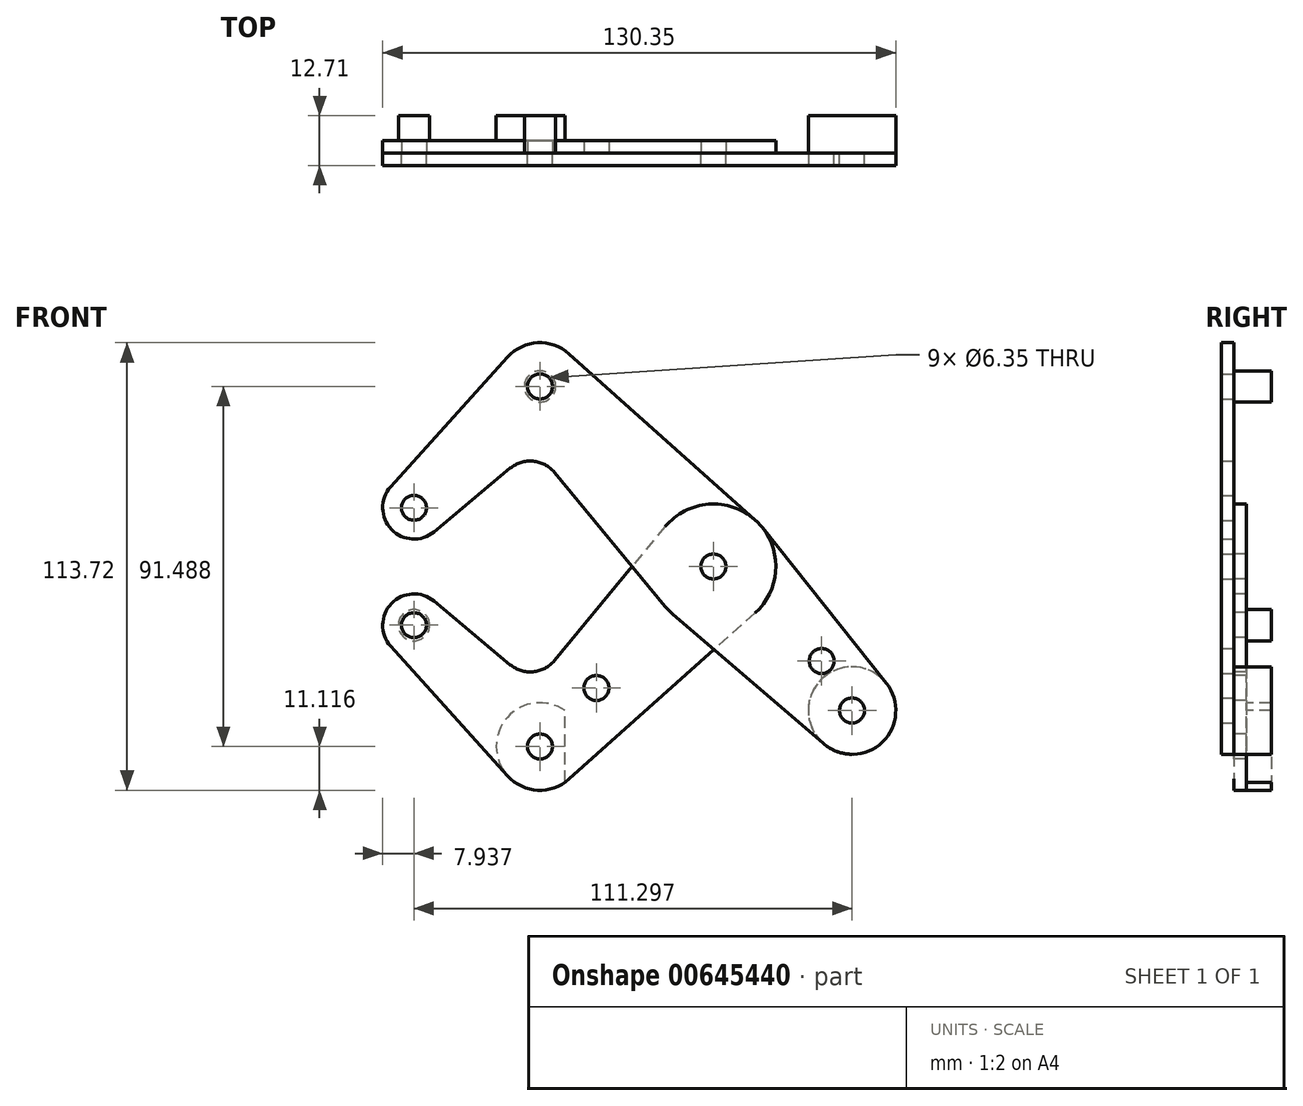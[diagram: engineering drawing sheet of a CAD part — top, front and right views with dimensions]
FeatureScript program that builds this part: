
annotation { "Feature Type Name" : "Feature", "Feature Type Description" : "" }
export const myFeature = defineFeature(function(context is Context, id is Id, definition is map)
    precondition{}
    {
        {
            var Q0;
            Q0=qCreatedBy(makeId("Front.planeOp"),FACE);
            var sketch = newSketch(context, id + "F0", { "sketchPlane" : qUnion([Q0])});
            skCircle(sketch, "E0", {"center": v(0, 0) * mm, "radius": 15.88 * mm});
            skCircle(sketch, "E1", {"center": v(0, 0) * mm, "radius": 3.98 * mm});
            skCircle(sketch, "E2", {"center": v(0, 0) * mm, "radius": 3.18 * mm});
            skCircle(sketch, "E3", {"center": v(-44.04, 45.74) * mm, "radius": 11.11 * mm});
            skCircle(sketch, "E4", {"center": v(-44.04, 45.74) * mm, "radius": 3.18 * mm});
            skCircle(sketch, "E5", {"center": v(-76.06, 14.91) * mm, "radius": 7.94 * mm});
            skCircle(sketch, "E6", {"center": v(-76.06, 14.91) * mm, "radius": 3.18 * mm});
            skCircle(sketch, "E7", {"center": v(35.23, -36.6) * mm, "radius": 11.11 * mm});
            skCircle(sketch, "E8", {"center": v(35.23, -36.6) * mm, "radius": 3.18 * mm});
            skLineSegment(sketch, "E9", {"start": v(-76.06, 14.91) * mm, "end": v(-44.04, 45.74) * mm, "construction": true});
            skLineSegment(sketch, "E10", {"start": v(-44.04, 45.74) * mm, "end": v(35.23, -36.6) * mm, "construction": true});
            skCircle(sketch, "E11", {"center": v(27.52, -24.01) * mm, "radius": 3.18 * mm});
            skLineSegment(sketch, "E12", {"start": v(-81.96, 20.22) * mm, "end": v(-52.3, 53.18) * mm});
            skLineSegment(sketch, "E13", {"start": v(-70.98, 8.82) * mm, "end": v(-51.62, 24.96) * mm});
            skLineSegment(sketch, "E14", {"start": v(-36.64, 54.03) * mm, "end": v(10.58, 11.84) * mm});
            skLineSegment(sketch, "E15", {"start": v(-40.4, 23.92) * mm, "end": v(-12.23, -10.12) * mm});
            skLineSegment(sketch, "E16", {"start": v(-10.35, -12.03) * mm, "end": v(27.99, -45.02) * mm});
            skLineSegment(sketch, "E17", {"start": v(12.42, 9.9) * mm, "end": v(43.93, -29.67) * mm});
            skLineSegment(sketch, "E18", {"start": v(0, 0) * mm, "end": v(-44.04, -45.74) * mm, "construction": true});
            skLineSegment(sketch, "E19", {"start": v(-44.04, -45.74) * mm, "end": v(-76.06, -14.91) * mm, "construction": true});
            skCircle(sketch, "E20", {"center": v(-44.04, -45.74) * mm, "radius": 11.11 * mm});
            skCircle(sketch, "E21", {"center": v(-44.04, -45.74) * mm, "radius": 3.18 * mm});
            skCircle(sketch, "E22", {"center": v(-76.06, -14.91) * mm, "radius": 7.94 * mm});
            skCircle(sketch, "E23", {"center": v(-76.06, -14.91) * mm, "radius": 3.18 * mm});
            skCircle(sketch, "E24", {"center": v(-29.72, -30.87) * mm, "radius": 3.18 * mm});
            skLineSegment(sketch, "E25", {"start": v(-81.96, -20.22) * mm, "end": v(-52.3, -53.18) * mm});
            skLineSegment(sketch, "E26", {"start": v(-70.98, -8.82) * mm, "end": v(-51.62, -24.96) * mm});
            skArc(sketch, "E27.filletArc", {"start": v(-40.4, 23.92) * mm, "mid": v(-45.8, 26.77) * mm, "end": v(-51.62, 24.96) * mm});
            skLineSegment(sketch, "E28", {"start": v(-12.23, 10.12) * mm, "end": v(-40.4, -23.92) * mm});
            skLineSegment(sketch, "E29", {"start": v(10.58, -11.84) * mm, "end": v(-36.64, -54.03) * mm});
            skArc(sketch, "E30.filletArc", {"start": v(-51.62, -24.96) * mm, "mid": v(-45.8, -26.77) * mm, "end": v(-40.4, -23.92) * mm});
            skSolve(sketch);
        }
        {
            var Q0;
            {var subQ0=sQuery(id+"F0.wireOp",EDGE,"E12");Q0=makeQuery(id+"F0.imprint","IMPRINT",FACE,{"disambiguationData":[TD([[makeQuery(id+"F0.imprint","IMPRINT",EDGE,{"derivedFrom":subQ0}),-1.0]])]});}
            var Q1;
            Q1=makeQuery(id+"F0.imprint","IMPRINT",FACE,{"disambiguationData":[TD([[makeQuery(id+"F0.imprint","IMPRINT",EDGE,{"derivedFrom":sQuery(id+"F0.wireOp",EDGE,"E6")}),-1.0]])]});
            var Q2;
            {var subQ0=sQuery(id+"F0.wireOp",EDGE,"E15");var subQ1=sQuery(id+"F0.wireOp",EDGE,"E0");var subQ2=makeQuery(id+"F0.imprint","INTERSECT",VERTEX,{"derivedFrom":[subQ1,subQ0]});Q2=makeQuery(id+"F0.imprint","IMPRINT",FACE,{"disambiguationData":[TD([[makeQuery(id+"F0.imprint","IMPRINT",EDGE,{"disambiguationData":[TD([[subQ2,1.0]])],"derivedFrom":subQ1}),-1.0]])]});}
            var Q3;
            {var subQ0=sQuery(id+"F0.wireOp",EDGE,"E16");var subQ1=sQuery(id+"F0.wireOp",EDGE,"E0");var subQ2=makeQuery(id+"F0.imprint","INTERSECT",VERTEX,{"derivedFrom":[subQ1,subQ0]});Q3=makeQuery(id+"F0.imprint","IMPRINT",FACE,{"disambiguationData":[TD([[makeQuery(id+"F0.imprint","IMPRINT",EDGE,{"disambiguationData":[TD([[subQ2,-1.0]])],"derivedFrom":subQ1}),-1.0]])]});}
            var Q4;
            Q4=makeQuery(id+"F0.imprint","IMPRINT",FACE,{"disambiguationData":[TD([[makeQuery(id+"F0.imprint","IMPRINT",EDGE,{"derivedFrom":sQuery(id+"F0.wireOp",EDGE,"E1")}),-1.0]])]});
            var Q5;
            Q5=makeQuery(id+"F0.imprint","IMPRINT",FACE,{"disambiguationData":[TD([[makeQuery(id+"F0.imprint","IMPRINT",EDGE,{"derivedFrom":sQuery(id+"F0.wireOp",EDGE,"E1")}),1.0]])]});
            var Q6;
            Q6=makeQuery(id+"F0.imprint","IMPRINT",FACE,{"disambiguationData":[TD([[makeQuery(id+"F0.imprint","IMPRINT",EDGE,{"derivedFrom":sQuery(id+"F0.wireOp",EDGE,"E11")}),-1.0]])]});
            var Q7;
            Q7=makeQuery(id+"F0.imprint","IMPRINT",FACE,{"disambiguationData":[TD([[makeQuery(id+"F0.imprint","IMPRINT",EDGE,{"derivedFrom":sQuery(id+"F0.wireOp",EDGE,"E8")}),-1.0]])]});
            var Q8;
            Q8=makeQuery(id+"F0.imprint","IMPRINT",FACE,{"disambiguationData":[TD([[makeQuery(id+"F0.imprint","IMPRINT",EDGE,{"derivedFrom":sQuery(id+"F0.wireOp",EDGE,"E4")}),-1.0]])]});
            extrude(context, id + "F1", {"entities" : qUnion([Q0, Q1, Q2, Q3, Q4, Q5, Q6, Q7, Q8]), "depth" : 3.17 * mm, "offsetDistance" : 25.4 * mm});
        }
        {
            var Q0;
            Q0=makeQuery(id+"F0.imprint","IMPRINT",FACE,{"disambiguationData":[TD([[makeQuery(id+"F0.imprint","IMPRINT",EDGE,{"derivedFrom":sQuery(id+"F0.wireOp",EDGE,"E23")}),-1.0]])]});
            var Q1;
            Q1=makeQuery(id+"F0.imprint","IMPRINT",FACE,{"disambiguationData":[TD([[makeQuery(id+"F0.imprint","IMPRINT",EDGE,{"derivedFrom":sQuery(id+"F0.wireOp",EDGE,"E24")}),-1.0]])]});
            var Q2;
            Q2=makeQuery(id+"F0.imprint","IMPRINT",FACE,{"disambiguationData":[TD([[makeQuery(id+"F0.imprint","IMPRINT",EDGE,{"derivedFrom":sQuery(id+"F0.wireOp",EDGE,"E21")}),-1.0]])]});
            var Q3;
            {var subQ0=sQuery(id+"F0.wireOp",EDGE,"E16");var subQ1=sQuery(id+"F0.wireOp",EDGE,"E0");var subQ2=makeQuery(id+"F0.imprint","INTERSECT",VERTEX,{"derivedFrom":[subQ1,subQ0]});Q3=makeQuery(id+"F0.imprint","IMPRINT",FACE,{"disambiguationData":[TD([[makeQuery(id+"F0.imprint","IMPRINT",EDGE,{"disambiguationData":[TD([[subQ2,-1.0]])],"derivedFrom":subQ1}),-1.0]])]});}
            var Q4;
            {var subQ0=sQuery(id+"F0.wireOp",EDGE,"E15");var subQ1=sQuery(id+"F0.wireOp",EDGE,"E0");var subQ2=makeQuery(id+"F0.imprint","INTERSECT",VERTEX,{"derivedFrom":[subQ1,subQ0]});Q4=makeQuery(id+"F0.imprint","IMPRINT",FACE,{"disambiguationData":[TD([[makeQuery(id+"F0.imprint","IMPRINT",EDGE,{"disambiguationData":[TD([[subQ2,1.0]])],"derivedFrom":subQ1}),-1.0]])]});}
            var Q5;
            Q5=makeQuery(id+"F0.imprint","IMPRINT",FACE,{"disambiguationData":[TD([[makeQuery(id+"F0.imprint","IMPRINT",EDGE,{"derivedFrom":sQuery(id+"F0.wireOp",EDGE,"E1")}),-1.0]])]});
            var Q6;
            Q6=makeQuery(id+"F0.imprint","IMPRINT",FACE,{"disambiguationData":[TD([[makeQuery(id+"F0.imprint","IMPRINT",EDGE,{"derivedFrom":sQuery(id+"F0.wireOp",EDGE,"E1")}),1.0]])]});
            extrude(context, id + "F2", {"entities" : qUnion([Q0, Q1, Q2, Q3, Q4, Q5, Q6]), "oppositeDirection" : true, "depth" : 3.17 * mm, "offsetDistance" : 25.4 * mm});
        }
        {
            var Q0;
            Q0=makeQuery(id+"F1.opExtrude","CAP_FACE",FACE,{"disambiguationData":[OSD([sQuery(id+"F0.wireOp",EDGE,"E0"),sQuery(id+"F0.wireOp",EDGE,"E2"),sQuery(id+"F0.wireOp",EDGE,"E3"),sQuery(id+"F0.wireOp",EDGE,"E4"),sQuery(id+"F0.wireOp",EDGE,"E5"),sQuery(id+"F0.wireOp",EDGE,"E6"),sQuery(id+"F0.wireOp",EDGE,"E7"),sQuery(id+"F0.wireOp",EDGE,"E8"),sQuery(id+"F0.wireOp",EDGE,"E11"),sQuery(id+"F0.wireOp",EDGE,"E12"),sQuery(id+"F0.wireOp",EDGE,"E13"),sQuery(id+"F0.wireOp",EDGE,"E14"),sQuery(id+"F0.wireOp",EDGE,"E15"),sQuery(id+"F0.wireOp",EDGE,"E16"),sQuery(id+"F0.wireOp",EDGE,"E17"),sQuery(id+"F0.wireOp",EDGE,"E27.filletArc")])],"isStart":false});
            var sketch = newSketch(context, id + "F3", { "sketchPlane" : qUnion([Q0])});
            skCircle(sketch, "E31", {"center": v(-44.04, 45.74) * mm, "radius": 3.98 * mm});
            skCircle(sketch, "E32.0", {"center": v(35.23, -36.6) * mm, "radius": 11.11 * mm});
            skSolve(sketch);
        }
        {
            var Q0;
            Q0=makeQuery(id+"F0.imprint","IMPRINT",FACE,{"disambiguationData":[TD([[makeQuery(id+"F0.imprint","IMPRINT",EDGE,{"derivedFrom":sQuery(id+"F0.wireOp",EDGE,"E23")}),-1.0]])]});
            var sketch = newSketch(context, id + "F4", { "sketchPlane" : qUnion([Q0])});
            skCircle(sketch, "E33", {"center": v(-76.06, -14.91) * mm, "radius": 3.98 * mm});
            skArc(sketch, "E34.0", {"start": v(-37.7, -36.62) * mm, "mid": v(-55.16, -45.74) * mm, "end": v(-37.7, -54.86) * mm});
            skLineSegment(sketch, "E35", {"start": v(-44.04, -45.74) * mm, "end": v(35.23, -36.6) * mm, "construction": true});
            skLineSegment(sketch, "E36", {"start": v(-37.7, -36.62) * mm, "end": v(-37.7, -54.86) * mm});
            skSolve(sketch);
        }
        {
            var Q0;
            Q0=qCreatedBy(makeId("Front.planeOp"),FACE);
            cPlane(context, id + "F5", {"entities" : qUnion([Q0]), "cplaneType" : CPlaneType.OFFSET, "offset" : 9.52 * mm, "oppositeDirection" : true, "width" : 152.4 * mm, "height" : 152.4 * mm});
        }
        {
            var Q0;
            Q0 = qSketchRegion(id + "F3", true);
            var Q1;
            Q1 = qSketchRegion(id + "F4", true);
            var Q2;
            Q2=qCreatedBy(id+"F5.planeOp",FACE);
            extrude(context, id + "F6", {"entities" : qUnion([Q0, Q1]), "endBound" : BoundingType.UP_TO_SURFACE, "oppositeDirection" : true, "depth" : 25.4 * mm, "endBoundEntityFace" : qUnion([Q2]), "offsetDistance" : 25.4 * mm});
        }
        {
            var Q0;
            Q0=makeQuery(id+"F1.opExtrude","SWEPT_BODY",BODY,{"disambiguationData":[OSD([sQuery(id+"F0.wireOp",EDGE,"E0"),sQuery(id+"F0.wireOp",EDGE,"E2"),sQuery(id+"F0.wireOp",EDGE,"E3"),sQuery(id+"F0.wireOp",EDGE,"E4"),sQuery(id+"F0.wireOp",EDGE,"E5"),sQuery(id+"F0.wireOp",EDGE,"E6"),sQuery(id+"F0.wireOp",EDGE,"E7"),sQuery(id+"F0.wireOp",EDGE,"E8"),sQuery(id+"F0.wireOp",EDGE,"E11"),sQuery(id+"F0.wireOp",EDGE,"E12"),sQuery(id+"F0.wireOp",EDGE,"E13"),sQuery(id+"F0.wireOp",EDGE,"E14"),sQuery(id+"F0.wireOp",EDGE,"E15"),sQuery(id+"F0.wireOp",EDGE,"E16"),sQuery(id+"F0.wireOp",EDGE,"E17"),sQuery(id+"F0.wireOp",EDGE,"E27.filletArc")])]});
            var Q1;
            Q1=makeQuery(id+"F2.opExtrude","SWEPT_BODY",BODY,{"disambiguationData":[OSD([sQuery(id+"F0.wireOp",EDGE,"E0"),sQuery(id+"F0.wireOp",EDGE,"E2"),sQuery(id+"F0.wireOp",EDGE,"E20"),sQuery(id+"F0.wireOp",EDGE,"E21"),sQuery(id+"F0.wireOp",EDGE,"E22"),sQuery(id+"F0.wireOp",EDGE,"E23"),sQuery(id+"F0.wireOp",EDGE,"E24"),sQuery(id+"F0.wireOp",EDGE,"E25"),sQuery(id+"F0.wireOp",EDGE,"E26"),sQuery(id+"F0.wireOp",EDGE,"E28"),sQuery(id+"F0.wireOp",EDGE,"E29"),sQuery(id+"F0.wireOp",EDGE,"E30.filletArc")])]});
            var Q2;
            Q2=makeQuery(id+"F6.opExtrude","SWEPT_BODY",BODY,{"disambiguationData":[OSD([sQuery(id+"F3.wireOp",EDGE,"E32.0")])]});
            var Q3;
            Q3=makeQuery(id+"F6.opExtrude","SWEPT_BODY",BODY,{"disambiguationData":[OSD([sQuery(id+"F3.wireOp",EDGE,"E31")])]});
            var Q4;
            Q4=makeQuery(id+"F6.opExtrude","SWEPT_BODY",BODY,{"disambiguationData":[OSD([sQuery(id+"F4.wireOp",EDGE,"E33")])]});
            var Q5;
            Q5=makeQuery(id+"F6.opExtrude","SWEPT_BODY",BODY,{"disambiguationData":[OSD([sQuery(id+"F4.wireOp",EDGE,"E34.0"),sQuery(id+"F4.wireOp",EDGE,"E36")])]});
            booleanBodies(context, id + "F7", {"operationType" : BooleanOperationType.SUBTRACTION, "tools" : qUnion([Q0, Q1]), "targets" : qUnion([Q2, Q3, Q4, Q5]), "keepTools" : true});
        }
    });
